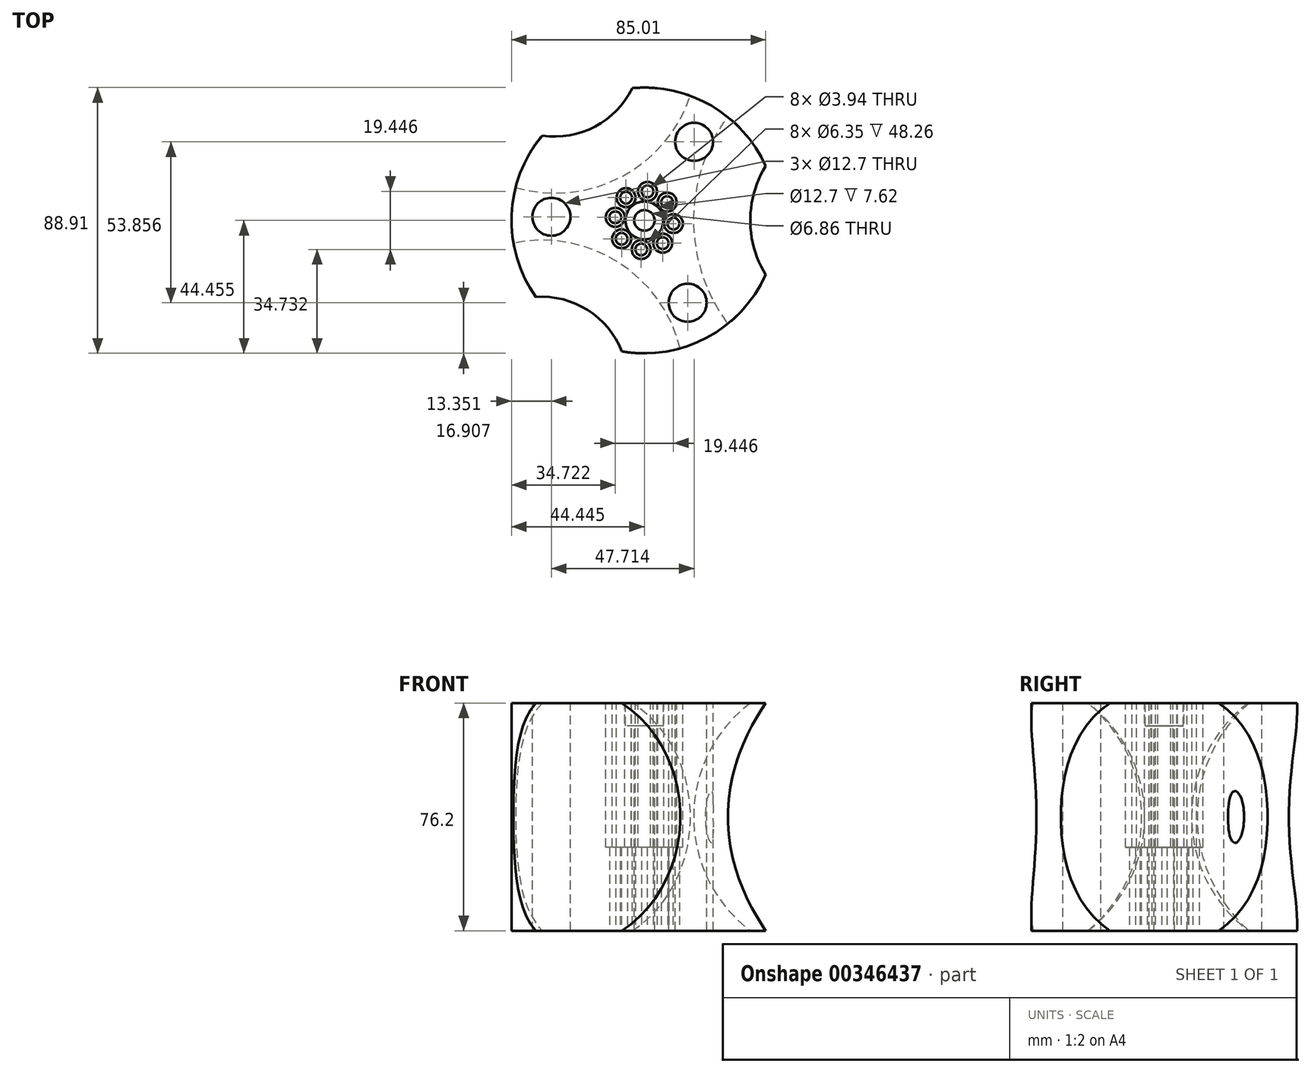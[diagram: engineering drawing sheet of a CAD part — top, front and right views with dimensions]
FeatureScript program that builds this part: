
annotation { "Feature Type Name" : "Feature", "Feature Type Description" : "" }
export const myFeature = defineFeature(function(context is Context, id is Id, definition is map)
    precondition{}
    {
        {
            var Q0;
            Q0=qCreatedBy(makeId("Top.planeOp"),FACE);
            var sketch = newSketch(context, id + "F0", { "sketchPlane" : qUnion([Q0])});
            skCircle(sketch, "E0", {"center": v(-96.8, 47.63) * mm, "radius": 44.45 * mm});
            skCircle(sketch, "E1", {"center": v(-96.8, 47.63) * mm, "radius": 16.51 * mm});
            skCircle(sketch, "E2", {"center": v(-96.8, 47.63) * mm, "radius": 9.78 * mm});
            skCircle(sketch, "E3", {"center": v(-89.18, 53.76) * mm, "radius": 1.97 * mm});
            skCircle(sketch, "E4.1.0", {"center": v(-95.75, 57.35) * mm, "radius": 1.97 * mm});
            skCircle(sketch, "E4.2.0", {"center": v(-102.93, 55.24) * mm, "radius": 1.97 * mm});
            skCircle(sketch, "E4.3.0", {"center": v(-106.52, 48.67) * mm, "radius": 1.97 * mm});
            skCircle(sketch, "E4.4.0", {"center": v(-104.41, 41.5) * mm, "radius": 1.97 * mm});
            skCircle(sketch, "E4.5.0", {"center": v(-97.84, 37.9) * mm, "radius": 1.97 * mm});
            skCircle(sketch, "E4.6.0", {"center": v(-90.66, 40) * mm, "radius": 1.97 * mm});
            skCircle(sketch, "E4.7.0", {"center": v(-87.07, 46.58) * mm, "radius": 1.97 * mm});
            skSolve(sketch);
        }
        {
            var Q0;
            Q0=makeQuery(id+"F0.imprint","IMPRINT",FACE,{"disambiguationData":[TD([[makeQuery(id+"F0.imprint","IMPRINT",EDGE,{"derivedFrom":sQuery(id+"F0.wireOp",EDGE,"E0")}),1.0]])]});
            var Q1;
            Q1=makeQuery(id+"F0.imprint","IMPRINT",FACE,{"disambiguationData":[TD([[makeQuery(id+"F0.imprint","IMPRINT",EDGE,{"derivedFrom":sQuery(id+"F0.wireOp",EDGE,"E1")}),1.0]])]});
            var Q2;
            {var subQ1=sQuery(id+"F0.wireOp",EDGE,"E2");var subQ4=sQuery(id+"F0.wireOp",EDGE,"E3");var subQ5=makeQuery(id+"F0.imprint","INTERSECT",VERTEX,{"disambiguationData":[OD(0.0)],"derivedFrom":[subQ1,subQ4]});Q2=makeQuery(id+"F0.imprint","IMPRINT",FACE,{"disambiguationData":[TD([[makeQuery(id+"F0.imprint","IMPRINT",EDGE,{"disambiguationData":[TD([[subQ5,1.0]])],"derivedFrom":subQ1}),1.0]])]});}
            extrude(context, id + "F1", {"entities" : qUnion([Q0, Q1, Q2]), "depth" : 38.1 * mm, "hasSecondDirection" : true, "secondDirectionOppositeDirection" : true, "secondDirectionDepth" : 38.1 * mm});
        }
        {
            var Q0;
            Q0=qCreatedBy(makeId("Top.planeOp"),FACE);
            var sketch = newSketch(context, id + "F2", { "sketchPlane" : qUnion([Q0])});
            skCircle(sketch, "E5.0.0", {"center": v(-96.8, 47.63) * mm, "radius": 44.45 * mm});
            skCircle(sketch, "E6", {"center": v(-96.8, 47.63) * mm, "radius": 16.51 * mm});
            skLineSegment(sketch, "E7", {"start": v(-32.58, 47.63) * mm, "end": v(-32.58, 95.38) * mm});
            skLineSegment(sketch, "E8", {"start": v(-32.58, -0.13) * mm, "end": v(-32.58, 95.38) * mm});
            skLineSegment(sketch, "E9", {"start": v(-32.58, 47.63) * mm, "end": v(-32.58, -9.52) * mm});
            skLineSegment(sketch, "E10", {"start": v(-32.58, 47.63) * mm, "end": v(-32.58, 104.78) * mm});
            skPoint(sketch, "E11", {"position": v(-80.34, 45.07) * mm});
            skArc(sketch, "E12", {"start": v(-32.58, -9.52) * mm, "mid": v(15.17, 47.63) * mm, "end": v(-32.58, 104.78) * mm});
            skPoint(sketch, "E13", {"position": v(15.17, 47.63) * mm});
            skLineSegment(sketch, "E14", {"start": v(-96.8, 47.63) * mm, "end": v(-44.42, 47.63) * mm, "construction": true});
            skLineSegment(sketch, "E15", {"start": v(-96.8, 47.63) * mm, "end": v(-126.31, -3.5) * mm, "construction": true});
            skLineSegment(sketch, "E16", {"start": v(-32.58, 47.63) * mm, "end": v(-19.5, 47.63) * mm});
            skArc(sketch, "E17.1.0", {"start": v(-79.4, 131.8) * mm, "mid": v(-152.78, 144.59) * mm, "end": v(-178.4, 74.66) * mm});
            skLineSegment(sketch, "E17.1.1", {"start": v(-128.9, 103.23) * mm, "end": v(-79.4, 131.8) * mm});
            skLineSegment(sketch, "E17.1.2", {"start": v(-128.9, 103.23) * mm, "end": v(-178.4, 74.66) * mm});
            skArc(sketch, "E17.2.0", {"start": v(-178.4, 20.6) * mm, "mid": v(-152.78, -49.34) * mm, "end": v(-79.4, -36.56) * mm});
            skLineSegment(sketch, "E17.2.1", {"start": v(-128.9, -7.98) * mm, "end": v(-178.4, 20.6) * mm});
            skLineSegment(sketch, "E17.2.2", {"start": v(-128.9, -7.98) * mm, "end": v(-79.4, -36.56) * mm});
            skLineSegment(sketch, "E18", {"start": v(-88.25, 33.5) * mm, "end": v(-45.7, -40.2) * mm});
            skSolve(sketch);
        }
        {
            var Q0;
            {var subQ5=sQuery(id+"F2.wireOp",EDGE,"E12");Q0=makeQuery(id+"F2.imprint","IMPRINT",FACE,{"disambiguationData":[TD([[makeQuery(id+"F2.imprint","IMPRINT",EDGE,{"derivedFrom":subQ5}),1.0]])]});}
            var Q1;
            {var subQ0=sQuery(id+"F2.wireOp",EDGE,"E10");var subQ1=sQuery(id+"F2.wireOp",EDGE,"aOpEJ7Df-Mzx5-U4IW-AKo9-5E0Zru6Bx9m7");var subQ2=makeQuery(id+"F2.imprint","INTERSECT",VERTEX,{"derivedFrom":[subQ1,subQ0]});Q1=makeQuery(id+"F2.imprint","IMPRINT",FACE,{"disambiguationData":[TD([[makeQuery(id+"F2.imprint","IMPRINT",EDGE,{"disambiguationData":[TD([[subQ2,1.0]])],"derivedFrom":subQ1}),1.0]])]});}
            var Q2;
            Q2=sQuery(id+"F2.wireOp",EDGE,"aOpEJ7Df-Mzx5-U4IW-AKo9-5E0Zru6Bx9m7");
            var Q3;
            Q3=sQuery(id+"F2.wireOp",EDGE,"E9");
            revolve(context, id + "F3", {"operationType" : NewBodyOperationType.REMOVE, "entities" : qUnion([Q0, Q1]), "surfaceEntities" : qUnion([Q2]), "axis" : qUnion([Q3]), "revolveType" : RevolveType.FULL, "oppositeDirection" : true});
        }
        {
            var Q0;
            Q0=qCreatedBy(makeId("Top.planeOp"),FACE);
            var sketch = newSketch(context, id + "F4", { "sketchPlane" : qUnion([Q0])});
            skLineSegment(sketch, "E19.0", {"start": v(-131.12, -6.7) * mm, "end": v(-173.82, 14.66) * mm});
            skLineSegment(sketch, "E20.0", {"start": v(-88.4, -28.07) * mm, "end": v(-131.12, -6.7) * mm});
            skArc(sketch, "E21.0", {"start": v(-173.82, 14.66) * mm, "mid": v(-152.48, -49.41) * mm, "end": v(-88.4, -28.07) * mm});
            skSolve(sketch);
        }
        {
            var Q0;
            Q0=qSketchRegion(id+"F4",true);
            var Q1;
            Q1=sQuery(id+"F4.wireOp",EDGE,"E19.0");
            revolve(context, id + "F5", {"operationType" : NewBodyOperationType.REMOVE, "entities" : qUnion([Q0]), "axis" : qUnion([Q1]), "revolveType" : RevolveType.FULL, "oppositeDirection" : true});
        }
        {
            var Q0;
            Q0=qCreatedBy(makeId("Top.planeOp"),FACE);
            var sketch = newSketch(context, id + "F6", { "sketchPlane" : qUnion([Q0])});
            skLineSegment(sketch, "E22", {"start": v(-170.33, 85.13) * mm, "end": v(-126.68, 104.51) * mm});
            skLineSegment(sketch, "E23", {"start": v(-126.68, 104.51) * mm, "end": v(-83.04, 123.9) * mm});
            skArc(sketch, "E24", {"start": v(-83.04, 123.9) * mm, "mid": v(-146.07, 148.15) * mm, "end": v(-170.33, 85.13) * mm});
            skSolve(sketch);
        }
        {
            var Q0;
            Q0=qSketchRegion(id+"F6",true);
            var Q1;
            Q1=sQuery(id+"F6.wireOp",EDGE,"E22");
            revolve(context, id + "F7", {"operationType" : NewBodyOperationType.REMOVE, "entities" : qUnion([Q0]), "axis" : qUnion([Q1]), "revolveType" : RevolveType.FULL, "oppositeDirection" : true});
        }
        {
            var Q0;
            Q0=makeQuery(id+"F1.opExtrude","CAP_FACE",FACE,{"disambiguationData":[OSD([sQuery(id+"F0.wireOp",EDGE,"E0"),sQuery(id+"F0.wireOp",EDGE,"E3"),sQuery(id+"F0.wireOp",EDGE,"E4.1.0"),sQuery(id+"F0.wireOp",EDGE,"E4.2.0"),sQuery(id+"F0.wireOp",EDGE,"E4.3.0"),sQuery(id+"F0.wireOp",EDGE,"E4.4.0"),sQuery(id+"F0.wireOp",EDGE,"E4.5.0"),sQuery(id+"F0.wireOp",EDGE,"E4.6.0"),sQuery(id+"F0.wireOp",EDGE,"E4.7.0")])],"isStart":false});
            var sketch = newSketch(context, id + "F8", { "sketchPlane" : qUnion([Q0])});
            skCircle(sketch, "E25.0", {"center": v(-102.93, 55.24) * mm, "radius": 1.97 * mm});
            skCircle(sketch, "E26", {"center": v(-102.93, 55.24) * mm, "radius": 3.18 * mm});
            skCircle(sketch, "E27.1.0", {"center": v(-95.75, 57.35) * mm, "radius": 3.18 * mm});
            skCircle(sketch, "E27.2.0", {"center": v(-89.18, 53.76) * mm, "radius": 3.18 * mm});
            skCircle(sketch, "E27.3.0", {"center": v(-87.07, 46.58) * mm, "radius": 3.18 * mm});
            skCircle(sketch, "E27.4.0", {"center": v(-90.66, 40) * mm, "radius": 3.18 * mm});
            skCircle(sketch, "E27.5.0", {"center": v(-97.84, 37.9) * mm, "radius": 3.18 * mm});
            skCircle(sketch, "E27.6.0", {"center": v(-104.41, 41.5) * mm, "radius": 3.18 * mm});
            skCircle(sketch, "E27.7.0", {"center": v(-106.52, 48.67) * mm, "radius": 3.18 * mm});
            skPoint(sketch, "E27.center", {"position": v(-96.8, 47.63) * mm});
            skLineSegment(sketch, "E27.anchor1", {"start": v(-96.8, 47.63) * mm, "end": v(-102.93, 55.24) * mm, "construction": true});
            skLineSegment(sketch, "E27.anchor2", {"start": v(-96.8, 47.63) * mm, "end": v(-106.52, 48.67) * mm, "construction": true});
            skSolve(sketch);
        }
        {
            var Q0;
            Q0=makeQuery(id+"F8.imprint","IMPRINT",FACE,{"disambiguationData":[TD([[makeQuery(id+"F8.imprint","IMPRINT",EDGE,{"derivedFrom":sQuery(id+"F8.wireOp",EDGE,"E25.0")}),-1.0]])]});
            var Q1;
            Q1=makeQuery(id+"F8.imprint","IMPRINT",FACE,{"disambiguationData":[TD([[makeQuery(id+"F8.imprint","IMPRINT",EDGE,{"derivedFrom":sQuery(id+"F8.wireOp",EDGE,"E27.1.0")}),1.0]])]});
            var Q2;
            Q2=makeQuery(id+"F8.imprint","IMPRINT",FACE,{"disambiguationData":[TD([[makeQuery(id+"F8.imprint","IMPRINT",EDGE,{"derivedFrom":sQuery(id+"F8.wireOp",EDGE,"E27.2.0")}),1.0]])]});
            var Q3;
            Q3=makeQuery(id+"F8.imprint","IMPRINT",FACE,{"disambiguationData":[TD([[makeQuery(id+"F8.imprint","IMPRINT",EDGE,{"derivedFrom":sQuery(id+"F8.wireOp",EDGE,"E27.3.0")}),1.0]])]});
            var Q4;
            Q4=makeQuery(id+"F8.imprint","IMPRINT",FACE,{"disambiguationData":[TD([[makeQuery(id+"F8.imprint","IMPRINT",EDGE,{"derivedFrom":sQuery(id+"F8.wireOp",EDGE,"E27.4.0")}),1.0]])]});
            var Q5;
            Q5=makeQuery(id+"F8.imprint","IMPRINT",FACE,{"disambiguationData":[TD([[makeQuery(id+"F8.imprint","IMPRINT",EDGE,{"derivedFrom":sQuery(id+"F8.wireOp",EDGE,"E27.5.0")}),1.0]])]});
            var Q6;
            Q6=makeQuery(id+"F8.imprint","IMPRINT",FACE,{"disambiguationData":[TD([[makeQuery(id+"F8.imprint","IMPRINT",EDGE,{"derivedFrom":sQuery(id+"F8.wireOp",EDGE,"E27.6.0")}),1.0]])]});
            var Q7;
            Q7=makeQuery(id+"F8.imprint","IMPRINT",FACE,{"disambiguationData":[TD([[makeQuery(id+"F8.imprint","IMPRINT",EDGE,{"derivedFrom":sQuery(id+"F8.wireOp",EDGE,"E27.7.0")}),1.0]])]});
            var Q8;
            Q8=sQuery(id+"F8.wireOp",EDGE,"E26");
            var Q9;
            Q9=sQuery(id+"F8.wireOp",EDGE,"E27.1.0");
            var Q10;
            Q10=sQuery(id+"F8.wireOp",EDGE,"E27.2.0");
            var Q11;
            Q11=sQuery(id+"F8.wireOp",EDGE,"E27.3.0");
            var Q12;
            Q12=sQuery(id+"F8.wireOp",EDGE,"E27.4.0");
            var Q13;
            Q13=sQuery(id+"F8.wireOp",EDGE,"E27.5.0");
            var Q14;
            Q14=sQuery(id+"F8.wireOp",EDGE,"E27.6.0");
            var Q15;
            Q15=sQuery(id+"F8.wireOp",EDGE,"E27.7.0");
            extrude(context, id + "F9", {"entities" : qUnion([Q0, Q1, Q2, Q3, Q4, Q5, Q6, Q7]), "operationType" : NewBodyOperationType.REMOVE, "surfaceEntities" : qUnion([Q8, Q9, Q10, Q11, Q12, Q13, Q14, Q15]), "oppositeDirection" : true, "depth" : 48.26 * mm});
        }
        {
            var Q0;
            Q0=makeQuery(id+"F1.opExtrude","CAP_FACE",FACE,{"disambiguationData":[OSD([sQuery(id+"F0.wireOp",EDGE,"E0"),sQuery(id+"F0.wireOp",EDGE,"E3"),sQuery(id+"F0.wireOp",EDGE,"E4.1.0"),sQuery(id+"F0.wireOp",EDGE,"E4.2.0"),sQuery(id+"F0.wireOp",EDGE,"E4.3.0"),sQuery(id+"F0.wireOp",EDGE,"E4.4.0"),sQuery(id+"F0.wireOp",EDGE,"E4.5.0"),sQuery(id+"F0.wireOp",EDGE,"E4.6.0"),sQuery(id+"F0.wireOp",EDGE,"E4.7.0")])],"isStart":false});
            var sketch = newSketch(context, id + "F10", { "sketchPlane" : qUnion([Q0])});
            skCircle(sketch, "E28", {"center": v(-96.8, 47.63) * mm, "radius": 6.35 * mm});
            skSolve(sketch);
        }
        {
            var Q0;
            Q0=qSketchRegion(id+"F10",true);
            extrude(context, id + "F11", {"entities" : qUnion([Q0]), "operationType" : NewBodyOperationType.REMOVE, "oppositeDirection" : true, "depth" : 7.62 * mm});
        }
        {
            var Q0;
            Q0=makeQuery(id+"F11.boolean.opBoolean","COPY",FACE,{"derivedFrom":makeQuery(id+"F11.opExtrude","CAP_FACE",FACE,{"disambiguationData":[OSD([sQuery(id+"F10.wireOp",EDGE,"E28")])],"isStart":false})});
            var sketch = newSketch(context, id + "F12", { "sketchPlane" : qUnion([Q0])});
            skCircle(sketch, "E29", {"center": v(-96.8, 47.63) * mm, "radius": 3.43 * mm});
            skSolve(sketch);
        }
        {
            var Q0;
            Q0=makeQuery(id+"F12.imprint","IMPRINT",FACE,{"disambiguationData":[TD([[makeQuery(id+"F12.imprint","IMPRINT",EDGE,{"derivedFrom":sQuery(id+"F12.wireOp",EDGE,"E29")}),1.0]])]});
            extrude(context, id + "F13", {"entities" : qUnion([Q0]), "operationType" : NewBodyOperationType.REMOVE, "endBound" : BoundingType.UP_TO_NEXT, "oppositeDirection" : true, "depth" : 25.4 * mm});
        }
        {
            var Q0;
            Q0=makeQuery(id+"F1.opExtrude","CAP_FACE",FACE,{"disambiguationData":[OSD([sQuery(id+"F0.wireOp",EDGE,"E0"),sQuery(id+"F0.wireOp",EDGE,"E3"),sQuery(id+"F0.wireOp",EDGE,"E4.1.0"),sQuery(id+"F0.wireOp",EDGE,"E4.2.0"),sQuery(id+"F0.wireOp",EDGE,"E4.3.0"),sQuery(id+"F0.wireOp",EDGE,"E4.4.0"),sQuery(id+"F0.wireOp",EDGE,"E4.5.0"),sQuery(id+"F0.wireOp",EDGE,"E4.6.0"),sQuery(id+"F0.wireOp",EDGE,"E4.7.0")])],"isStart":false});
            var sketch = newSketch(context, id + "F14", { "sketchPlane" : qUnion([Q0])});
            skLineSegment(sketch, "E30", {"start": v(-96.8, 47.63) * mm, "end": v(-69.66, 90.57) * mm});
            skCircle(sketch, "E31", {"center": v(-80.17, 73.93) * mm, "radius": 6.35 * mm});
            skCircle(sketch, "E32.1.0", {"center": v(-127.89, 48.86) * mm, "radius": 6.35 * mm});
            skCircle(sketch, "E32.2.0", {"center": v(-82.32, 20.08) * mm, "radius": 6.35 * mm});
            skPoint(sketch, "E32.center", {"position": v(-96.8, 47.63) * mm});
            skSolve(sketch);
        }
        {
            var Q0;
            Q0=makeQuery(id+"F14.imprint","IMPRINT",FACE,{"disambiguationData":[TD([[makeQuery(id+"F14.imprint","IMPRINT",EDGE,{"derivedFrom":sQuery(id+"F14.wireOp",EDGE,"E32.1.0")}),1.0]])]});
            var Q1;
            {var subQ0=sQuery(id+"F14.wireOp",EDGE,"E31");var subQ1=sQuery(id+"F14.wireOp",EDGE,"E30");var subQ2=makeQuery(id+"F14.imprint","INTERSECT",VERTEX,{"disambiguationData":[OD(0.0)],"derivedFrom":[subQ1,subQ0]});Q1=makeQuery(id+"F14.imprint","IMPRINT",FACE,{"disambiguationData":[TD([[makeQuery(id+"F14.imprint","IMPRINT",EDGE,{"disambiguationData":[TD([[subQ2,-1.0]])],"derivedFrom":subQ1}),1.0]])]});}
            var Q2;
            {var subQ0=sQuery(id+"F14.wireOp",EDGE,"E31");var subQ1=sQuery(id+"F14.wireOp",EDGE,"E30");var subQ2=makeQuery(id+"F14.imprint","INTERSECT",VERTEX,{"disambiguationData":[OD(0.0)],"derivedFrom":[subQ1,subQ0]});Q2=makeQuery(id+"F14.imprint","IMPRINT",FACE,{"disambiguationData":[TD([[makeQuery(id+"F14.imprint","IMPRINT",EDGE,{"disambiguationData":[TD([[subQ2,-1.0]])],"derivedFrom":subQ1}),-1.0]])]});}
            var Q3;
            Q3=makeQuery(id+"F14.imprint","IMPRINT",FACE,{"disambiguationData":[TD([[makeQuery(id+"F14.imprint","IMPRINT",EDGE,{"derivedFrom":sQuery(id+"F14.wireOp",EDGE,"E32.2.0")}),1.0]])]});
            extrude(context, id + "F15", {"entities" : qUnion([Q0, Q1, Q2, Q3]), "operationType" : NewBodyOperationType.REMOVE, "endBound" : BoundingType.UP_TO_NEXT, "oppositeDirection" : true, "depth" : 25.4 * mm});
        }
    });
